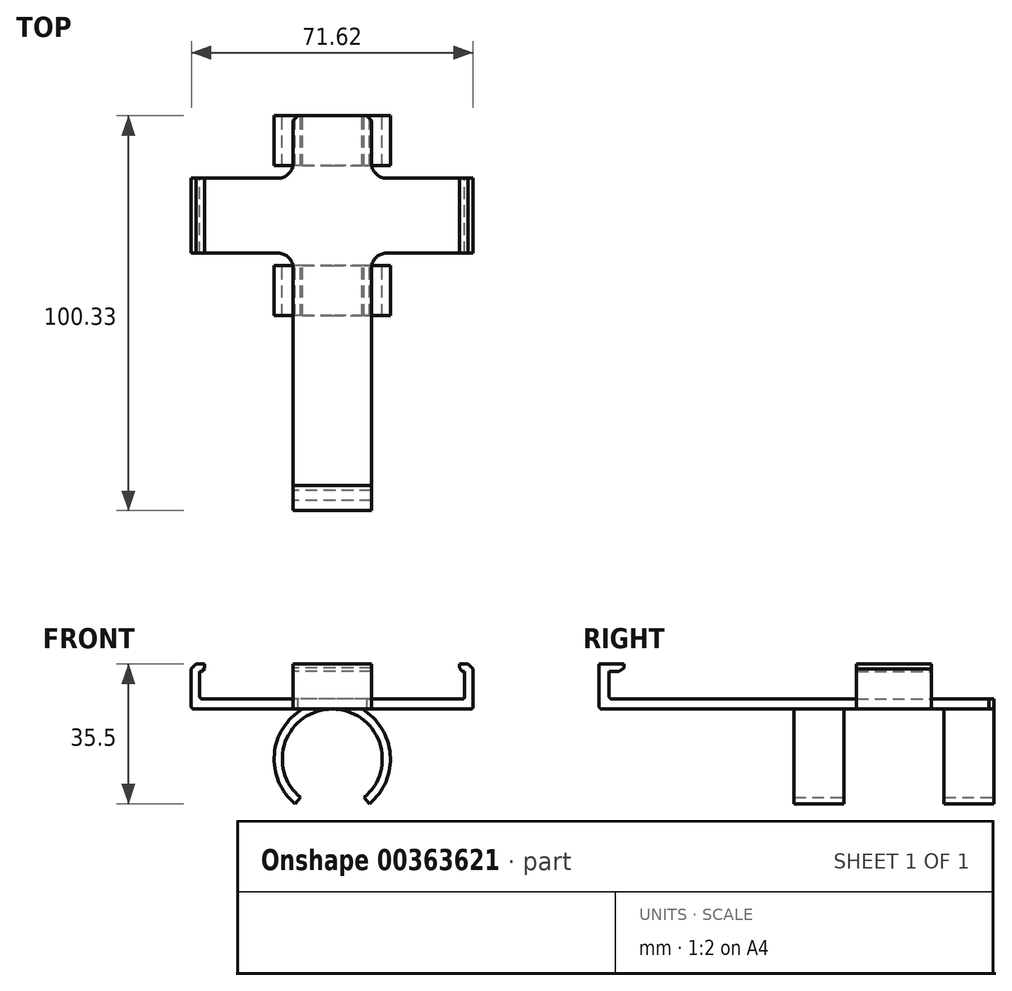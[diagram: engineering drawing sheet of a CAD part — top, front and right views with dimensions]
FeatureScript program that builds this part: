
annotation { "Feature Type Name" : "Feature", "Feature Type Description" : "" }
export const myFeature = defineFeature(function(context is Context, id is Id, definition is map)
    precondition{}
    {
        {
            var Q0;
            Q0=qCreatedBy(makeId("Front.planeOp"),FACE);
            var sketch = newSketch(context, id + "F0", { "sketchPlane" : qUnion([Q0])});
            skArc(sketch, "E0", {"start": v(9.41, -11.37) * mm, "mid": v(0, 14.76) * mm, "end": v(-9.41, -11.37) * mm});
            skArc(sketch, "E1", {"start": v(8.1, -9.78) * mm, "mid": v(0, 12.7) * mm, "end": v(-8.1, -9.78) * mm});
            skLineSegment(sketch, "E2", {"start": v(-8.1, -9.78) * mm, "end": v(-9.41, -11.37) * mm});
            skLineSegment(sketch, "E3", {"start": v(8.1, -9.78) * mm, "end": v(9.41, -11.37) * mm});
            skLineSegment(sketch, "E4", {"start": v(0, 0) * mm, "end": v(0, -14.76) * mm, "construction": true});
            skSolve(sketch);
        }
        {
            var Q0;
            Q0=qSketchRegion(id+"F0",true);
            extrude(context, id + "F1", {"entities" : qUnion([Q0]), "depth" : 25.4 * mm, "hasSecondDirection" : true, "secondDirectionOppositeDirection" : true, "secondDirectionDepth" : 25.4 * mm});
        }
        {
            var Q0;
            Q0=qCreatedBy(makeId("Right.planeOp"),FACE);
            var sketch = newSketch(context, id + "F2", { "sketchPlane" : qUnion([Q0])});
            skLineSegment(sketch, "E5.bottom", {"start": v(-12.7, 21.65) * mm, "end": v(12.7, 21.65) * mm});
            skLineSegment(sketch, "E5.top", {"start": v(-12.7, -19.3) * mm, "end": v(12.7, -19.3) * mm});
            skLineSegment(sketch, "E5.left", {"start": v(-12.7, 21.65) * mm, "end": v(-12.7, -19.3) * mm});
            skLineSegment(sketch, "E5.right", {"start": v(12.7, 21.65) * mm, "end": v(12.7, -19.3) * mm});
            skSolve(sketch);
        }
        {
            var Q0;
            Q0=qSketchRegion(id+"F2",true);
            extrude(context, id + "F3", {"entities" : qUnion([Q0]), "operationType" : NewBodyOperationType.REMOVE, "oppositeDirection" : true, "depth" : 25.4 * mm, "hasSecondDirection" : true, "secondDirectionOppositeDirection" : false, "secondDirectionDepth" : 25.4 * mm});
        }
        {
            var Q0;
            Q0=qCreatedBy(makeId("Front.planeOp"),FACE);
            var sketch = newSketch(context, id + "F4", { "sketchPlane" : qUnion([Q0])});
            skLineSegment(sketch, "E6", {"start": v(0, 12.7) * mm, "end": v(0, 14.76) * mm, "construction": true});
            skLineSegment(sketch, "E7.rect.bottom", {"start": v(9.97, 12.7) * mm, "end": v(-9.97, 12.7) * mm});
            skLineSegment(sketch, "E7.rect.top", {"start": v(9.97, 15.24) * mm, "end": v(-9.97, 15.24) * mm});
            skLineSegment(sketch, "E7.rect.left", {"start": v(9.97, 12.7) * mm, "end": v(9.97, 15.24) * mm});
            skLineSegment(sketch, "E7.rect.right", {"start": v(-9.97, 12.7) * mm, "end": v(-9.97, 15.24) * mm});
            skPoint(sketch, "E7.rect.middle", {"position": v(0, 13.97) * mm});
            skSolve(sketch);
        }
        {
            var Q0;
            Q0=qSketchRegion(id+"F4",true);
            extrude(context, id + "F5", {"entities" : qUnion([Q0]), "operationType" : NewBodyOperationType.ADD, "depth" : 25.4 * mm, "hasSecondDirection" : true, "secondDirectionOppositeDirection" : true, "secondDirectionDepth" : 25.4 * mm});
        }
        {
            var Q0;
            Q0=qCreatedBy(makeId("Front.planeOp"),FACE);
            var sketch = newSketch(context, id + "F6", { "sketchPlane" : qUnion([Q0])});
            skLineSegment(sketch, "E8.rect.bottom", {"start": v(0, 12.7) * mm, "end": v(-33.66, 12.7) * mm});
            skLineSegment(sketch, "E8.rect.top", {"start": v(0, 15.24) * mm, "end": v(-33.02, 15.24) * mm});
            skPoint(sketch, "E8.rect.middle", {"position": v(0, 13.97) * mm});
            skLineSegment(sketch, "E9.bottom", {"start": v(-33.66, 12.7) * mm, "end": v(-35.18, 12.7) * mm});
            skLineSegment(sketch, "E9.left", {"start": v(-33.66, 15.87) * mm, "end": v(-33.65, 22.23) * mm});
            skLineSegment(sketch, "E9.right", {"start": v(-35.81, 13.33) * mm, "end": v(-35.81, 22.23) * mm});
            skPoint(sketch, "E10.visualSharp", {"position": v(-33.66, 15.24) * mm});
            skArc(sketch, "E10.filletArc", {"start": v(-33.66, 15.87) * mm, "mid": v(-33.47, 15.43) * mm, "end": v(-33.02, 15.24) * mm});
            skPoint(sketch, "E11.visualSharp", {"position": v(-35.81, 12.7) * mm});
            skArc(sketch, "E11.filletArc", {"start": v(-35.81, 13.33) * mm, "mid": v(-35.63, 12.89) * mm, "end": v(-35.18, 12.7) * mm});
            skLineSegment(sketch, "E12.bottom", {"start": v(-33.65, 22.23) * mm, "end": v(-33.36, 22.23) * mm});
            skLineSegment(sketch, "E12.top", {"start": v(-35.81, 24.13) * mm, "end": v(-32.39, 24.13) * mm});
            skLineSegment(sketch, "E12.left", {"start": v(-35.81, 22.23) * mm, "end": v(-35.81, 24.13) * mm});
            skLineSegment(sketch, "E12.right", {"start": v(-32.39, 23.18) * mm, "end": v(-32.39, 24.13) * mm});
            skLineSegment(sketch, "E13", {"start": v(-32.39, 23.18) * mm, "end": v(-32.83, 22.5) * mm});
            skPoint(sketch, "E14.orphan", {"position": v(-32.38, 22.23) * mm});
            skPoint(sketch, "E15.visualSharp", {"position": v(-33.02, 22.23) * mm});
            skArc(sketch, "E15.filletArc", {"start": v(-33.36, 22.23) * mm, "mid": v(-33.06, 22.3) * mm, "end": v(-32.83, 22.5) * mm});
            skLineSegment(sketch, "E16", {"start": v(0, 15.24) * mm, "end": v(0, 12.7) * mm});
            skLineSegment(sketch, "E17.MirrorCS", {"start": v(0, 15.24) * mm, "end": v(33.02, 15.24) * mm});
            skLineSegment(sketch, "E18.MirrorCS", {"start": v(0, 12.7) * mm, "end": v(33.66, 12.7) * mm});
            skLineSegment(sketch, "E19.MirrorCS", {"start": v(33.66, 12.7) * mm, "end": v(35.18, 12.7) * mm});
            skArc(sketch, "E20.MirrorCS", {"start": v(35.81, 13.33) * mm, "mid": v(35.63, 12.89) * mm, "end": v(35.18, 12.7) * mm});
            skLineSegment(sketch, "E21.MirrorCS", {"start": v(35.81, 13.33) * mm, "end": v(35.81, 22.22) * mm});
            skArc(sketch, "E22.MirrorCS", {"start": v(33.66, 15.87) * mm, "mid": v(33.47, 15.43) * mm, "end": v(33.02, 15.24) * mm});
            skLineSegment(sketch, "E23.MirrorCS", {"start": v(33.66, 15.87) * mm, "end": v(33.65, 22.22) * mm});
            skLineSegment(sketch, "E24.MirrorCS", {"start": v(35.81, 22.22) * mm, "end": v(35.81, 24.13) * mm});
            skLineSegment(sketch, "E25.MirrorCS", {"start": v(35.81, 24.13) * mm, "end": v(32.39, 24.13) * mm});
            skLineSegment(sketch, "E26.MirrorCS", {"start": v(32.39, 23.18) * mm, "end": v(32.39, 24.13) * mm});
            skLineSegment(sketch, "E27.MirrorCS", {"start": v(32.39, 23.18) * mm, "end": v(32.83, 22.5) * mm});
            skArc(sketch, "E28.MirrorCS", {"start": v(33.36, 22.22) * mm, "mid": v(33.06, 22.3) * mm, "end": v(32.83, 22.5) * mm});
            skLineSegment(sketch, "E29.MirrorCS", {"start": v(33.66, 22.22) * mm, "end": v(33.36, 22.22) * mm});
            skSolve(sketch);
        }
        {
            var Q0;
            Q0=qSketchRegion(id+"F6",true);
            extrude(context, id + "F7", {"entities" : qUnion([Q0]), "operationType" : NewBodyOperationType.ADD, "depth" : 9.52 * mm, "hasSecondDirection" : true, "secondDirectionOppositeDirection" : true, "secondDirectionDepth" : 9.52 * mm});
        }
        {
            var Q0;
            Q0=makeQuery(id+"F7.boolean.opBoolean","INTERSECT",EDGE,{"derivedFrom":[makeQuery(id+"F5.opExtrude","SWEPT_FACE",FACE,{"disambiguationData":[OSD([sQuery(id+"F4.wireOp",EDGE,"E7.rect.right")])]}),makeQuery(id+"F7.opExtrude","CAP_FACE",FACE,{"disambiguationData":[OSD([sQuery(id+"F6.wireOp",EDGE,"E8.rect.bottom"),sQuery(id+"F6.wireOp",EDGE,"E8.rect.top"),sQuery(id+"F6.wireOp",EDGE,"E9.bottom"),sQuery(id+"F6.wireOp",EDGE,"E9.left"),sQuery(id+"F6.wireOp",EDGE,"E9.right"),sQuery(id+"F6.wireOp",EDGE,"E10.filletArc"),sQuery(id+"F6.wireOp",EDGE,"E11.filletArc"),sQuery(id+"F6.wireOp",EDGE,"E12.bottom"),sQuery(id+"F6.wireOp",EDGE,"E12.top"),sQuery(id+"F6.wireOp",EDGE,"E12.left"),sQuery(id+"F6.wireOp",EDGE,"E12.right"),sQuery(id+"F6.wireOp",EDGE,"E13"),sQuery(id+"F6.wireOp",EDGE,"E15.filletArc"),sQuery(id+"F6.wireOp",EDGE,"E17.MirrorCS"),sQuery(id+"F6.wireOp",EDGE,"E18.MirrorCS"),sQuery(id+"F6.wireOp",EDGE,"E19.MirrorCS"),sQuery(id+"F6.wireOp",EDGE,"E20.MirrorCS"),sQuery(id+"F6.wireOp",EDGE,"E21.MirrorCS"),sQuery(id+"F6.wireOp",EDGE,"E22.MirrorCS"),sQuery(id+"F6.wireOp",EDGE,"E23.MirrorCS"),sQuery(id+"F6.wireOp",EDGE,"E24.MirrorCS"),sQuery(id+"F6.wireOp",EDGE,"E25.MirrorCS"),sQuery(id+"F6.wireOp",EDGE,"E26.MirrorCS"),sQuery(id+"F6.wireOp",EDGE,"E27.MirrorCS"),sQuery(id+"F6.wireOp",EDGE,"E28.MirrorCS"),sQuery(id+"F6.wireOp",EDGE,"E29.MirrorCS")])],"isStart":true})]});
            var Q1;
            Q1=makeQuery(id+"F7.boolean.opBoolean","INTERSECT",EDGE,{"derivedFrom":[makeQuery(id+"F5.opExtrude","SWEPT_FACE",FACE,{"disambiguationData":[OSD([sQuery(id+"F4.wireOp",EDGE,"E7.rect.left")])]}),makeQuery(id+"F7.opExtrude","CAP_FACE",FACE,{"disambiguationData":[OSD([sQuery(id+"F6.wireOp",EDGE,"E8.rect.bottom"),sQuery(id+"F6.wireOp",EDGE,"E8.rect.top"),sQuery(id+"F6.wireOp",EDGE,"E9.bottom"),sQuery(id+"F6.wireOp",EDGE,"E9.left"),sQuery(id+"F6.wireOp",EDGE,"E9.right"),sQuery(id+"F6.wireOp",EDGE,"E10.filletArc"),sQuery(id+"F6.wireOp",EDGE,"E11.filletArc"),sQuery(id+"F6.wireOp",EDGE,"E12.bottom"),sQuery(id+"F6.wireOp",EDGE,"E12.top"),sQuery(id+"F6.wireOp",EDGE,"E12.left"),sQuery(id+"F6.wireOp",EDGE,"E12.right"),sQuery(id+"F6.wireOp",EDGE,"E13"),sQuery(id+"F6.wireOp",EDGE,"E15.filletArc"),sQuery(id+"F6.wireOp",EDGE,"E17.MirrorCS"),sQuery(id+"F6.wireOp",EDGE,"E18.MirrorCS"),sQuery(id+"F6.wireOp",EDGE,"E19.MirrorCS"),sQuery(id+"F6.wireOp",EDGE,"E20.MirrorCS"),sQuery(id+"F6.wireOp",EDGE,"E21.MirrorCS"),sQuery(id+"F6.wireOp",EDGE,"E22.MirrorCS"),sQuery(id+"F6.wireOp",EDGE,"E23.MirrorCS"),sQuery(id+"F6.wireOp",EDGE,"E24.MirrorCS"),sQuery(id+"F6.wireOp",EDGE,"E25.MirrorCS"),sQuery(id+"F6.wireOp",EDGE,"E26.MirrorCS"),sQuery(id+"F6.wireOp",EDGE,"E27.MirrorCS"),sQuery(id+"F6.wireOp",EDGE,"E28.MirrorCS"),sQuery(id+"F6.wireOp",EDGE,"E29.MirrorCS")])],"isStart":true})]});
            var Q2;
            Q2=makeQuery(id+"F7.boolean.opBoolean","INTERSECT",EDGE,{"derivedFrom":[makeQuery(id+"F5.opExtrude","SWEPT_FACE",FACE,{"disambiguationData":[OSD([sQuery(id+"F4.wireOp",EDGE,"E7.rect.left")])]}),makeQuery(id+"F7.opExtrude","CAP_FACE",FACE,{"disambiguationData":[OSD([sQuery(id+"F6.wireOp",EDGE,"E8.rect.bottom"),sQuery(id+"F6.wireOp",EDGE,"E8.rect.top"),sQuery(id+"F6.wireOp",EDGE,"E9.bottom"),sQuery(id+"F6.wireOp",EDGE,"E9.left"),sQuery(id+"F6.wireOp",EDGE,"E9.right"),sQuery(id+"F6.wireOp",EDGE,"E10.filletArc"),sQuery(id+"F6.wireOp",EDGE,"E11.filletArc"),sQuery(id+"F6.wireOp",EDGE,"E12.bottom"),sQuery(id+"F6.wireOp",EDGE,"E12.top"),sQuery(id+"F6.wireOp",EDGE,"E12.left"),sQuery(id+"F6.wireOp",EDGE,"E12.right"),sQuery(id+"F6.wireOp",EDGE,"E13"),sQuery(id+"F6.wireOp",EDGE,"E15.filletArc"),sQuery(id+"F6.wireOp",EDGE,"E17.MirrorCS"),sQuery(id+"F6.wireOp",EDGE,"E18.MirrorCS"),sQuery(id+"F6.wireOp",EDGE,"E19.MirrorCS"),sQuery(id+"F6.wireOp",EDGE,"E20.MirrorCS"),sQuery(id+"F6.wireOp",EDGE,"E21.MirrorCS"),sQuery(id+"F6.wireOp",EDGE,"E22.MirrorCS"),sQuery(id+"F6.wireOp",EDGE,"E23.MirrorCS"),sQuery(id+"F6.wireOp",EDGE,"E24.MirrorCS"),sQuery(id+"F6.wireOp",EDGE,"E25.MirrorCS"),sQuery(id+"F6.wireOp",EDGE,"E26.MirrorCS"),sQuery(id+"F6.wireOp",EDGE,"E27.MirrorCS"),sQuery(id+"F6.wireOp",EDGE,"E28.MirrorCS"),sQuery(id+"F6.wireOp",EDGE,"E29.MirrorCS")])],"isStart":false})]});
            var Q3;
            Q3=makeQuery(id+"F7.boolean.opBoolean","INTERSECT",EDGE,{"derivedFrom":[makeQuery(id+"F5.opExtrude","SWEPT_FACE",FACE,{"disambiguationData":[OSD([sQuery(id+"F4.wireOp",EDGE,"E7.rect.right")])]}),makeQuery(id+"F7.opExtrude","CAP_FACE",FACE,{"disambiguationData":[OSD([sQuery(id+"F6.wireOp",EDGE,"E8.rect.bottom"),sQuery(id+"F6.wireOp",EDGE,"E8.rect.top"),sQuery(id+"F6.wireOp",EDGE,"E9.bottom"),sQuery(id+"F6.wireOp",EDGE,"E9.left"),sQuery(id+"F6.wireOp",EDGE,"E9.right"),sQuery(id+"F6.wireOp",EDGE,"E10.filletArc"),sQuery(id+"F6.wireOp",EDGE,"E11.filletArc"),sQuery(id+"F6.wireOp",EDGE,"E12.bottom"),sQuery(id+"F6.wireOp",EDGE,"E12.top"),sQuery(id+"F6.wireOp",EDGE,"E12.left"),sQuery(id+"F6.wireOp",EDGE,"E12.right"),sQuery(id+"F6.wireOp",EDGE,"E13"),sQuery(id+"F6.wireOp",EDGE,"E15.filletArc"),sQuery(id+"F6.wireOp",EDGE,"E17.MirrorCS"),sQuery(id+"F6.wireOp",EDGE,"E18.MirrorCS"),sQuery(id+"F6.wireOp",EDGE,"E19.MirrorCS"),sQuery(id+"F6.wireOp",EDGE,"E20.MirrorCS"),sQuery(id+"F6.wireOp",EDGE,"E21.MirrorCS"),sQuery(id+"F6.wireOp",EDGE,"E22.MirrorCS"),sQuery(id+"F6.wireOp",EDGE,"E23.MirrorCS"),sQuery(id+"F6.wireOp",EDGE,"E24.MirrorCS"),sQuery(id+"F6.wireOp",EDGE,"E25.MirrorCS"),sQuery(id+"F6.wireOp",EDGE,"E26.MirrorCS"),sQuery(id+"F6.wireOp",EDGE,"E27.MirrorCS"),sQuery(id+"F6.wireOp",EDGE,"E28.MirrorCS"),sQuery(id+"F6.wireOp",EDGE,"E29.MirrorCS")])],"isStart":false})]});
            fillet(context, id + "F8", {"entities" : qUnion([Q0, Q1, Q2, Q3]), "radius" : 3.8 * mm, "tangentPropagation" : true, "allowEdgeOverflow" : false});
        }
        {
            var Q0;
            Q0=qCreatedBy(makeId("Right.planeOp"),FACE);
            var sketch = newSketch(context, id + "F9", { "sketchPlane" : qUnion([Q0])});
            skLineSegment(sketch, "E30.bottom", {"start": v(0, 12.7) * mm, "end": v(-72.4, 12.7) * mm});
            skLineSegment(sketch, "E30.top", {"start": v(0, 15.24) * mm, "end": v(-71.76, 15.24) * mm});
            skLineSegment(sketch, "E30.left", {"start": v(0, 12.7) * mm, "end": v(0, 15.24) * mm});
            skLineSegment(sketch, "E31.bottom", {"start": v(-72.4, 12.7) * mm, "end": v(-74.3, 12.7) * mm});
            skLineSegment(sketch, "E31.top", {"start": v(-72.4, 24.13) * mm, "end": v(-74.93, 24.13) * mm});
            skLineSegment(sketch, "E31.left", {"start": v(-72.4, 15.88) * mm, "end": v(-72.4, 22.23) * mm});
            skLineSegment(sketch, "E31.right", {"start": v(-74.93, 13.33) * mm, "end": v(-74.93, 24.13) * mm});
            skLineSegment(sketch, "E32.bottom", {"start": v(-74.93, 24.13) * mm, "end": v(-68.58, 24.13) * mm});
            skLineSegment(sketch, "E32.top", {"start": v(-72.4, 22.23) * mm, "end": v(-69.85, 22.23) * mm});
            skLineSegment(sketch, "E32.right", {"start": v(-68.58, 24.13) * mm, "end": v(-68.58, 23.18) * mm});
            skLineSegment(sketch, "E33", {"start": v(-68.58, 23.18) * mm, "end": v(-69.85, 22.23) * mm});
            skPoint(sketch, "E34.orphan", {"position": v(-68.58, 22.23) * mm});
            skPoint(sketch, "E35.visualSharp", {"position": v(-72.4, 15.24) * mm});
            skArc(sketch, "E35.filletArc", {"start": v(-72.4, 15.88) * mm, "mid": v(-72.2, 15.43) * mm, "end": v(-71.76, 15.24) * mm});
            skPoint(sketch, "E36.visualSharp", {"position": v(-74.93, 12.7) * mm});
            skArc(sketch, "E36.filletArc", {"start": v(-74.93, 13.33) * mm, "mid": v(-74.74, 12.89) * mm, "end": v(-74.3, 12.7) * mm});
            skSolve(sketch);
        }
        {
            var Q0;
            Q0=qSketchRegion(id+"F9",true);
            var Q1;
            {var subQ2=sQuery(id+"F4.wireOp",EDGE,"E7.rect.left");Q1=makeQuery(id+"F7.boolean.opBoolean","SPLIT",FACE,{"disambiguationData":[TD([makeQuery(id+"F1.opExtrude","CAP_FACE",FACE,{"disambiguationData":[OSD([sQuery(id+"F0.wireOp",EDGE,"E0"),sQuery(id+"F0.wireOp",EDGE,"E1"),sQuery(id+"F0.wireOp",EDGE,"E2"),sQuery(id+"F0.wireOp",EDGE,"E3")])],"isStart":false})])],"derivedFrom":makeQuery(id+"F5.opExtrude","SWEPT_FACE",FACE,{"disambiguationData":[OSD([subQ2])]})});}
            var Q2;
            {var subQ2=sQuery(id+"F4.wireOp",EDGE,"E7.rect.right");Q2=makeQuery(id+"F7.boolean.opBoolean","SPLIT",FACE,{"disambiguationData":[TD([makeQuery(id+"F1.opExtrude","CAP_FACE",FACE,{"disambiguationData":[OSD([sQuery(id+"F0.wireOp",EDGE,"E0"),sQuery(id+"F0.wireOp",EDGE,"E1"),sQuery(id+"F0.wireOp",EDGE,"E2"),sQuery(id+"F0.wireOp",EDGE,"E3")])],"isStart":false})])],"derivedFrom":makeQuery(id+"F5.opExtrude","SWEPT_FACE",FACE,{"disambiguationData":[OSD([subQ2])]})});}
            extrude(context, id + "F10", {"entities" : qUnion([Q0]), "operationType" : NewBodyOperationType.ADD, "endBound" : BoundingType.UP_TO_SURFACE, "endBoundEntityFace" : qUnion([Q1]), "depth" : 10.16 * mm, "hasSecondDirection" : true, "secondDirectionBound" : SecondDirectionBoundingType.UP_TO_SURFACE, "secondDirectionOppositeDirection" : true, "secondDirectionBoundEntityFace" : qUnion([Q2]), "secondDirectionDepth" : 6.35 * mm});
        }
        {
            var Q0;
            Q0=makeQuery(id+"F5.opExtrude","CAP_EDGE",EDGE,{"disambiguationData":[OSD([sQuery(id+"F4.wireOp",EDGE,"E7.rect.right")])],"isStart":true});
            var Q1;
            Q1=makeQuery(id+"F5.opExtrude","CAP_EDGE",EDGE,{"disambiguationData":[OSD([sQuery(id+"F4.wireOp",EDGE,"E7.rect.left")])],"isStart":true});
            chamfer(context, id + "F11", {"entities" : qUnion([Q0, Q1]), "width" : 1.27 * mm, "tangentPropagation" : true});
        }
        {
            var Q0;
            {var subQ0=sQuery(id+"F9.wireOp",EDGE,"E32.bottom");var subQ1=sQuery(id+"F9.wireOp",EDGE,"E31.right");Q0=makeQuery(id+"F10.opExtrude","TWEAK_EDGE",EDGE,{"derivedFrom":[makeQuery(id+"F9.imprint","IMPRINT",EDGE,{"derivedFrom":subQ1}),makeQuery(id+"F9.imprint","IMPRINT",EDGE,{"disambiguationData":[TD([[makeQuery(id+"F9.imprint","INTERSECT",VERTEX,{"derivedFrom":[subQ1,subQ0]}),-1.0]])],"derivedFrom":subQ0})]});}
            var Q1;
            Q1=makeQuery(id+"F7.opExtrude","SWEPT_EDGE",EDGE,{"disambiguationData":[OSD([sQuery(id+"F6.wireOp",EDGE,"E12.top"),sQuery(id+"F6.wireOp",EDGE,"E12.left")])]});
            var Q2;
            Q2=makeQuery(id+"F7.opExtrude","SWEPT_EDGE",EDGE,{"disambiguationData":[OSD([sQuery(id+"F6.wireOp",EDGE,"E24.MirrorCS"),sQuery(id+"F6.wireOp",EDGE,"E25.MirrorCS")])]});
            chamfer(context, id + "F12", {"entities" : qUnion([Q0, Q1, Q2]), "width" : 1.27 * mm, "tangentPropagation" : true});
        }
    });
